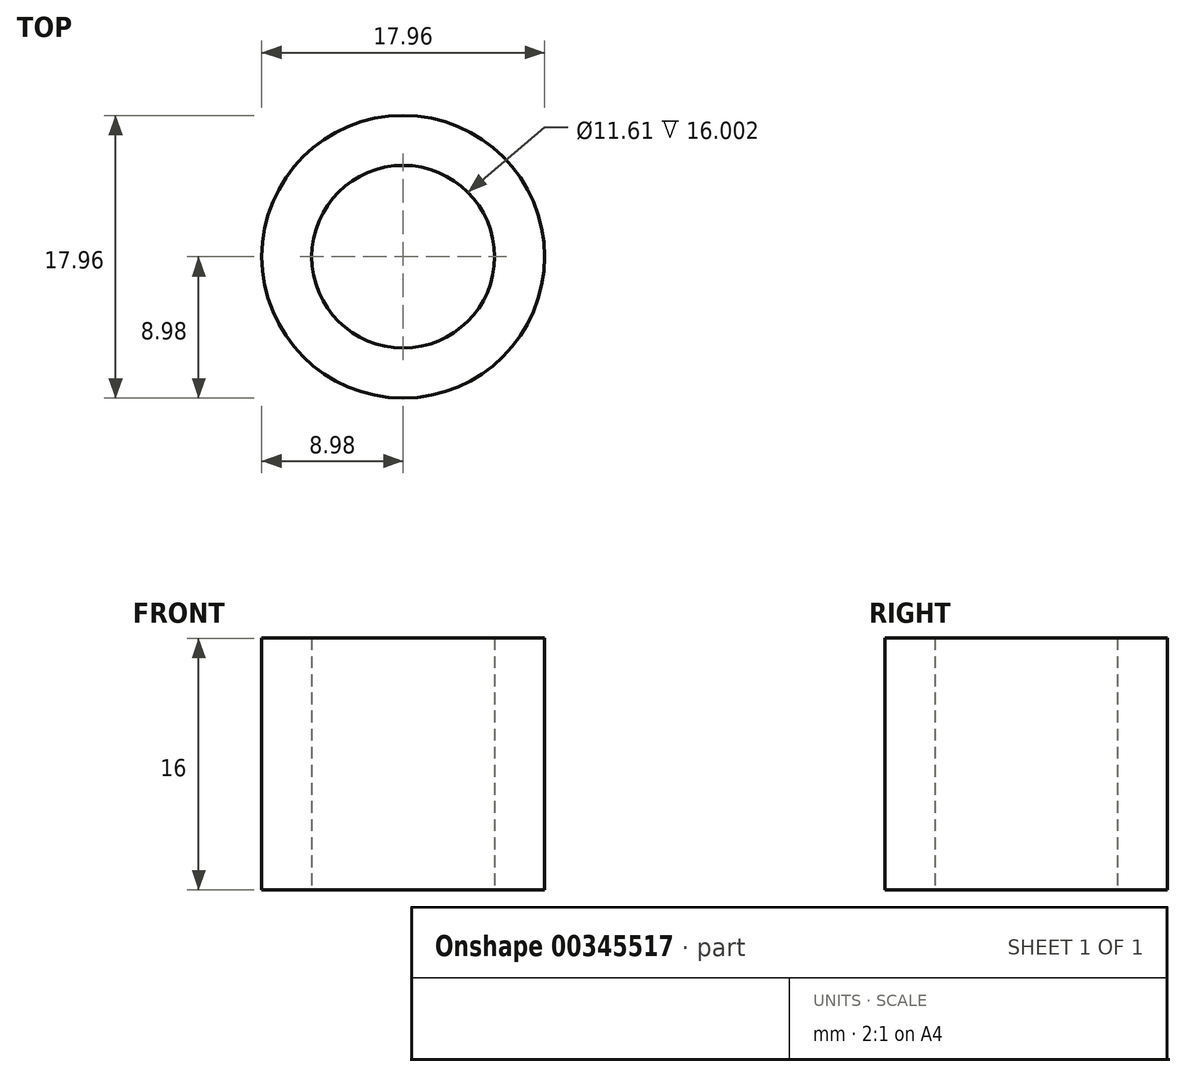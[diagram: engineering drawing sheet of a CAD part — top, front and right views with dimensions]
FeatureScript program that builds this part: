
annotation { "Feature Type Name" : "Feature", "Feature Type Description" : "" }
export const myFeature = defineFeature(function(context is Context, id is Id, definition is map)
    precondition{}
    {
        {
            var Q0;
            Q0=qCreatedBy(makeId("Top.planeOp"),FACE);
            var sketch = newSketch(context, id + "F0", { "sketchPlane" : qUnion([Q0])});
            skCircle(sketch, "E0", {"center": v(0, 0) * mm, "radius": 5.8 * mm});
            skCircle(sketch, "E1", {"center": v(0, 0) * mm, "radius": 8.98 * mm});
            skSolve(sketch);
        }
        {
            var Q0;
            Q0 = qSketchRegion(id + "F0", true);
            extrude(context, id + "F1", {"entities" : qUnion([Q0]), "depth" : 16 * mm});
        }
    });
